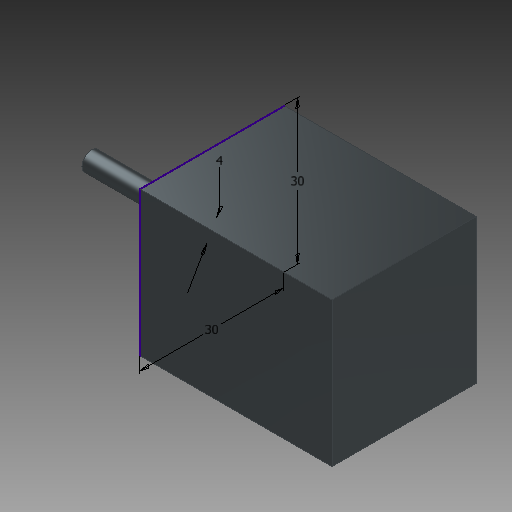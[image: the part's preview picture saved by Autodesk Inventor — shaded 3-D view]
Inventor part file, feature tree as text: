
AUTODESK INVENTOR PART (.ipt)
format: ipt  version: 2020 (Build 240168000, 168)  size: 96,256 bytes
history: native  units: mm
features: extrude x2, other x1, sketch x1
ambient origin geometry x8: Origin, YZ Plane, XZ Plane, XY Plane, X Axis, Y Axis, Z Axis, Center Point
bodies: Body1 (feature_tree)
feature tree (4):
  other  "Твердое тело1"
  sketch  "Эскиз1"
  extrude  "Выдавливание1"  Depth=30.0mm
  extrude  "Выдавливание2"  Depth=30.0mm
